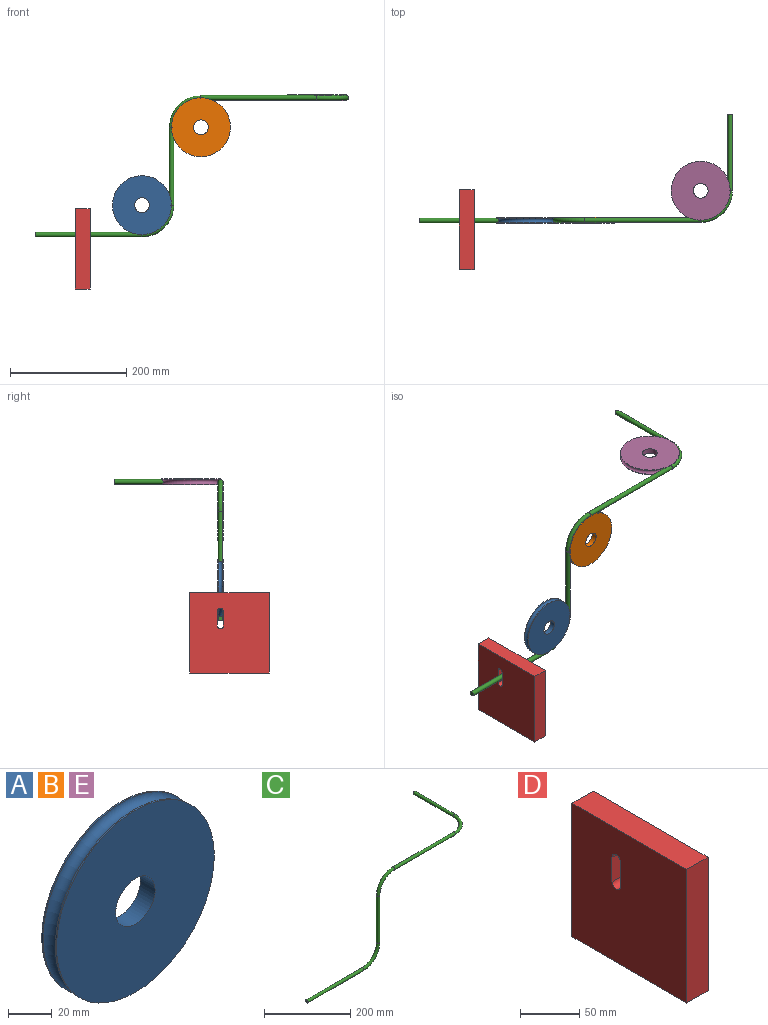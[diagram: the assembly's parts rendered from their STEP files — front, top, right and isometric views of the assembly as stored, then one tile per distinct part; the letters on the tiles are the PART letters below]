
ASSEMBLY  parts=5 mates=4
PART A: 6 faces, bbox 116.1x9.5x116.1 mm
  f0: cylinder r=50.8mm len=101.6mm, axis (0,-1,0), area 253.4mm2, adj f1,f5
  f1: torus R=50.8mm, axis (0,-1,0), area 3781.7mm2, adj f0,f2
  f2: cylinder r=50.8mm len=101.6mm, axis (0,-1,0), area 253.4mm2, adj f1,f3
  f3: plane 101.6x101.6mm, normal (0,-1,0), area 7600.6mm2, adj f2,f4
  f4: cylinder r=12.7mm len=25.4mm, axis (0,-1,0), area 760.1mm2, adj f3,f5
  f5: plane 101.6x101.6mm, normal (0,1,0), area 7600.6mm2, adj f0,f4
PART B: same geometry as A
PART C: 9 faces, bbox 543.7x190.7x252.8 mm
  f0: plane 7.94x7.94mm, normal (-1,0,0), area 49.5mm2, adj f2
  f1: plane 7.94x7.94mm, normal (0,1,0), area 49.5mm2, adj f8
  f2: cylinder r=3.97mm len=183.37mm, axis (1,0,0), area 4572.7mm2, adj f0,f3
  f3: torus R=50.8mm, axis (0,-1,0), area 1989.8mm2, adj f2,f4
  f4: cylinder r=3.97mm len=134.24mm, axis (0,0,1), area 3347.4mm2, adj f3,f5
  f5: torus R=50.8mm, axis (0,1,0), area 1989.8mm2, adj f4,f6
  f6: cylinder r=3.97mm len=199.44mm, axis (1,0,0), area 4973.2mm2, adj f5,f7
  f7: torus R=50.8mm, axis (0,0,1), area 1989.8mm2, adj f6,f8
  f8: cylinder r=3.97mm len=131.45mm, axis (0,1,0), area 3277.9mm2, adj f1,f7
PART D: 10 faces, bbox 25.4x137.5x138.4 mm
  f0: plane 138.35x137.49mm, normal (-1,0,0), area 18683.3mm2, adj f2,f3,f4,f5,f6,f7,f8,f9
  f1: plane 138.35x137.49mm, normal (1,0,0), area 18683.3mm2, adj f2,f3,f4,f5,f6,f7,f8,f9
  f2: plane 137.49x25.4mm, normal (0,0,1), area 3492.4mm2, adj f0,f1,f3,f5
  f3: plane 138.35x25.4mm, normal (0,-1,0), area 3514.1mm2, adj f0,f1,f2,f4
  f4: plane 137.49x25.4mm, normal (0,0,-1), area 3492.4mm2, adj f0,f1,f3,f5
  f5: plane 138.35x25.4mm, normal (0,1,0), area 3514.1mm2, adj f0,f1,f2,f4
  f6: cylinder r=5.08mm len=25.4mm, axis (-1,0,0), area 405.4mm2, adj f0,f1,f7,f9
  f7: plane 25.4x25.4mm, normal (0,1,0), area 645.2mm2, adj f0,f1,f6,f8
  f8: cylinder r=5.08mm len=25.4mm, axis (-1,0,0), area 405.4mm2, adj f0,f1,f7,f9
  f9: plane 25.4x25.4mm, normal (0,-1,0), area 645.2mm2, adj f0,f1,f6,f8
PART E: same geometry as A
PLACE A at identity fixed
PLACE B t=(101.6,0,134.24)mm
PLACE C t=(-183.37,0,-50.8)mm
PLACE D t=(-89.32,-22.38,-63.11)mm
PLACE E rot(axis=(-1,0,0),90deg) t=(301.03,50.8,185.04)mm
MATE fastened C.f7 <-> E.f0  axis (0,0,1) through (301.03,50.8,185.04)mm
MATE fastened C.f5 <-> B.f0  axis (0,1,0) through (101.6,0,134.24)mm
MATE fastened C.f3 <-> A.f0  axis (0,-1,0) through (0,0,0)mm
MATE slider C.f2 <-> D.f1  axis (-1,0,0) through (-183.37,0,-50.8)mm
